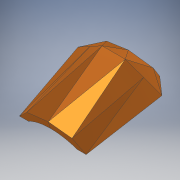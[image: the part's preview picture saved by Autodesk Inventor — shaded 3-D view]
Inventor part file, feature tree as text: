
AUTODESK INVENTOR PART (.ipt)
format: ipt  version: 2019 (Build 230136000, 136)  size: 174,080 bytes
history: native  units: mm
features: other x4, delete_face x1, direct_edit x1, plane x1
ambient origin geometry x8: Origin, YZ Plane, XZ Plane, XY Plane, X Axis, Y Axis, Z Axis, Center Point
bodies: Volumenkörper1 (feature_tree)
feature tree (7):
  other  "Main_afterRhino.ipt"
  delete_face  "Fläche löschen1"
  direct_edit  "Direktbearbeitung1"
  plane  "Arbeitsebene2"
  other  "Volumenkörper1::Main_afterRhino.ipt"
  other  "Bezeichnung1"
  other  "Skalierung1"
